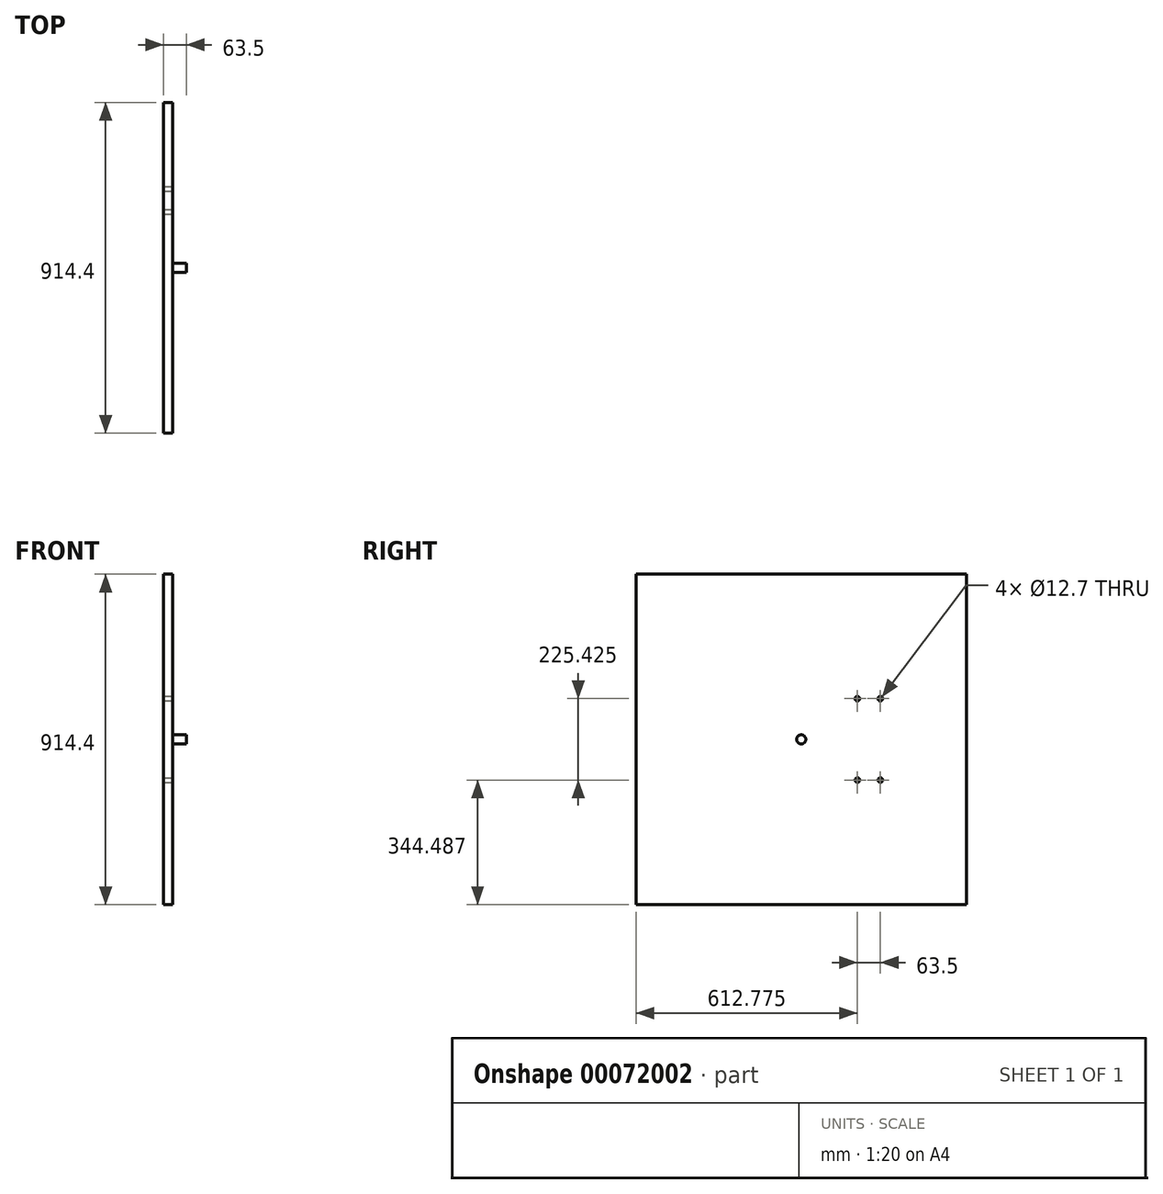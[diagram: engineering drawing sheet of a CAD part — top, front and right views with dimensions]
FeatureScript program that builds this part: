
annotation { "Feature Type Name" : "Feature", "Feature Type Description" : "" }
export const myFeature = defineFeature(function(context is Context, id is Id, definition is map)
    precondition{}
    {
        {
            var Q0;
            Q0=qCreatedBy(makeId("Right.planeOp"),FACE);
            var sketch = newSketch(context, id + "F0", { "sketchPlane" : qUnion([Q0])});
            skLineSegment(sketch, "E0.bottom", {"start": v(457.2, 457.2) * mm, "end": v(-457.2, 457.2) * mm});
            skLineSegment(sketch, "E0.top", {"start": v(457.2, -457.2) * mm, "end": v(-457.2, -457.2) * mm});
            skLineSegment(sketch, "E0.left", {"start": v(457.2, 457.2) * mm, "end": v(457.2, -457.2) * mm});
            skLineSegment(sketch, "E0.right", {"start": v(-457.2, 457.2) * mm, "end": v(-457.2, -457.2) * mm});
            skPoint(sketch, "E0.middle", {"position": v(0, 0) * mm});
            skSolve(sketch);
        }
        {
            var Q0;
            Q0=qSketchRegion(id+"F0",true);
            extrude(context, id + "F1", {"entities" : qUnion([Q0]), "depth" : 25.4 * mm});
        }
        {
            var Q0;
            Q0=makeQuery(id+"F1.opExtrude","CAP_FACE",FACE,{"disambiguationData":[OSD([sQuery(id+"F0.wireOp",EDGE,"E0.bottom"),sQuery(id+"F0.wireOp",EDGE,"E0.top"),sQuery(id+"F0.wireOp",EDGE,"E0.left"),sQuery(id+"F0.wireOp",EDGE,"E0.right")])],"isStart":false});
            var sketch = newSketch(context, id + "F2", { "sketchPlane" : qUnion([Q0])});
            skCircle(sketch, "E1", {"center": v(0, 0) * mm, "radius": 12.7 * mm});
            skSolve(sketch);
        }
        {
            var Q0;
            Q0=qSketchRegion(id+"F2",true);
            extrude(context, id + "F3", {"entities" : qUnion([Q0]), "operationType" : NewBodyOperationType.ADD, "depth" : 38.1 * mm});
        }
        {
            var Q0;
            Q0=makeQuery(id+"F1.opExtrude","CAP_FACE",FACE,{"disambiguationData":[OSD([sQuery(id+"F0.wireOp",EDGE,"E0.bottom"),sQuery(id+"F0.wireOp",EDGE,"E0.top"),sQuery(id+"F0.wireOp",EDGE,"E0.left"),sQuery(id+"F0.wireOp",EDGE,"E0.right")])],"isStart":false});
            var sketch = newSketch(context, id + "F4", { "sketchPlane" : qUnion([Q0])});
            skLineSegment(sketch, "E2.bottom", {"start": v(155.58, 112.71) * mm, "end": v(219.08, 112.71) * mm});
            skLineSegment(sketch, "E2.top", {"start": v(155.58, -112.71) * mm, "end": v(219.08, -112.71) * mm});
            skLineSegment(sketch, "E2.left", {"start": v(155.58, 112.71) * mm, "end": v(155.58, -112.71) * mm});
            skLineSegment(sketch, "E2.right", {"start": v(219.08, 112.71) * mm, "end": v(219.08, -112.71) * mm});
            skSolve(sketch);
        }
        {
            var Q0;
            Q0=sQuery(id+"F4.wireOp",VERTEX,"E2.left.start");
            var Q1;
            Q1=sQuery(id+"F4.wireOp",VERTEX,"E2.right.start");
            var Q2;
            Q2=sQuery(id+"F4.wireOp",VERTEX,"E2.left.end");
            var Q3;
            Q3=sQuery(id+"F4.wireOp",VERTEX,"E2.top.end");
            var Q4;
            Q4=makeQuery(id+"F1.opExtrude","SWEPT_BODY",BODY,{"disambiguationData":[OSD([sQuery(id+"F0.wireOp",EDGE,"E0.bottom"),sQuery(id+"F0.wireOp",EDGE,"E0.top"),sQuery(id+"F0.wireOp",EDGE,"E0.left"),sQuery(id+"F0.wireOp",EDGE,"E0.right")])]});
            hole(context, id + "F5", {"style" : HoleStyle.SIMPLE, "endStyle" : HoleEndStyle.THROUGH, "holeDiameter" : 12.7 * mm, "locations" : qUnion([Q0, Q1, Q2, Q3]), "scope" : qUnion([Q4]), "isTappedThrough" : true});
        }
    });
